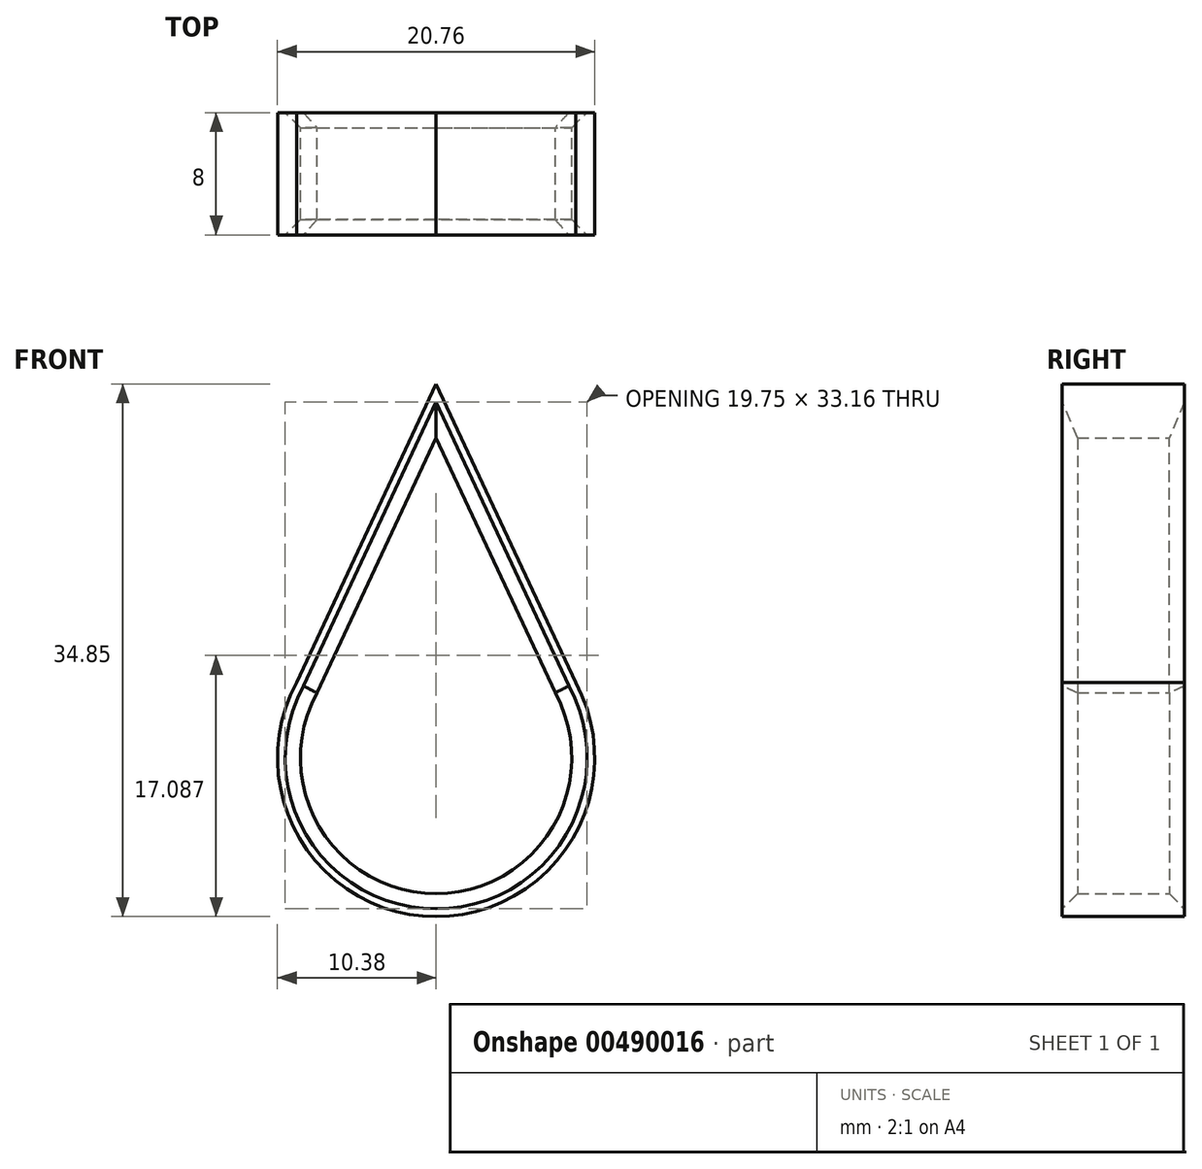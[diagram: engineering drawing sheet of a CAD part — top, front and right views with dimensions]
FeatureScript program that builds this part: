
annotation { "Feature Type Name" : "Feature", "Feature Type Description" : "" }
export const myFeature = defineFeature(function(context is Context, id is Id, definition is map)
    precondition{}
    {
        {
            var Q0;
            Q0=qCreatedBy(makeId("Front.planeOp"),FACE);
            var sketch = newSketch(context, id + "F0", { "sketchPlane" : qUnion([Q0])});
            skArc(sketch, "E0", {"start": v(-7.79, 4.26) * mm, "mid": v(0, -8.88) * mm, "end": v(7.79, 4.26) * mm});
            skArc(sketch, "E1.0", {"start": v(-9.13, 4.93) * mm, "mid": v(0, -10.37) * mm, "end": v(9.13, 4.93) * mm});
            skPoint(sketch, "E2", {"position": v(10.38, 0) * mm});
            skPoint(sketch, "E3", {"position": v(8.88, 0) * mm});
            skPoint(sketch, "E4", {"position": v(-8.88, 0) * mm});
            skPoint(sketch, "E5", {"position": v(-10.38, 0) * mm});
            skLineSegment(sketch, "E6", {"start": v(-8.26, 3.24) * mm, "end": v(0, 20.93) * mm});
            skLineSegment(sketch, "E7.MirrorCS", {"start": v(8.26, 3.24) * mm, "end": v(0, 20.93) * mm});
            skLineSegment(sketch, "E8.0", {"start": v(9.62, 3.88) * mm, "end": v(0, 24.47) * mm});
            skLineSegment(sketch, "E8.1", {"start": v(-9.62, 3.88) * mm, "end": v(0, 24.47) * mm});
            skSolve(sketch);
        }
        {
            var Q0;
            {var subQ0=sQuery(id+"F0.wireOp",EDGE,"E1.0");Q0=makeQuery(id+"F0.imprint","IMPRINT",FACE,{"disambiguationData":[TD([[makeQuery(id+"F0.imprint","IMPRINT",EDGE,{"derivedFrom":subQ0}),1.0]])]});}
            extrude(context, id + "F1", {"entities" : qUnion([Q0]), "depth" : 4 * mm, "offsetDistance" : 25 * mm, "hasSecondDirection" : true, "secondDirectionOppositeDirection" : true, "secondDirectionDepth" : 4 * mm});
        }
        {
            var Q0;
            Q0=makeQuery(id+"F1.opExtrude","CAP_EDGE",EDGE,{"disambiguationData":[OSD([sQuery(id+"F0.wireOp",EDGE,"E6")])],"isStart":false});
            var Q1;
            Q1=makeQuery(id+"F1.opExtrude","CAP_EDGE",EDGE,{"disambiguationData":[OSD([sQuery(id+"F0.wireOp",EDGE,"E0")])],"isStart":false});
            var Q2;
            Q2=makeQuery(id+"F1.opExtrude","CAP_EDGE",EDGE,{"disambiguationData":[OSD([sQuery(id+"F0.wireOp",EDGE,"E0")])],"isStart":true});
            var Q3;
            Q3=makeQuery(id+"F1.opExtrude","CAP_EDGE",EDGE,{"disambiguationData":[OSD([sQuery(id+"F0.wireOp",EDGE,"E6")])],"isStart":true});
            var Q4;
            Q4=makeQuery(id+"F1.opExtrude","CAP_EDGE",EDGE,{"disambiguationData":[OSD([sQuery(id+"F0.wireOp",EDGE,"E7.MirrorCS")])],"isStart":false});
            var Q5;
            Q5=makeQuery(id+"F1.opExtrude","CAP_EDGE",EDGE,{"disambiguationData":[OSD([sQuery(id+"F0.wireOp",EDGE,"E7.MirrorCS")])],"isStart":true});
            chamfer(context, id + "F2", {"entities" : qUnion([Q0, Q1, Q2, Q3, Q4, Q5]), "width" : 1 * mm, "tangentPropagation" : true});
        }
    });
